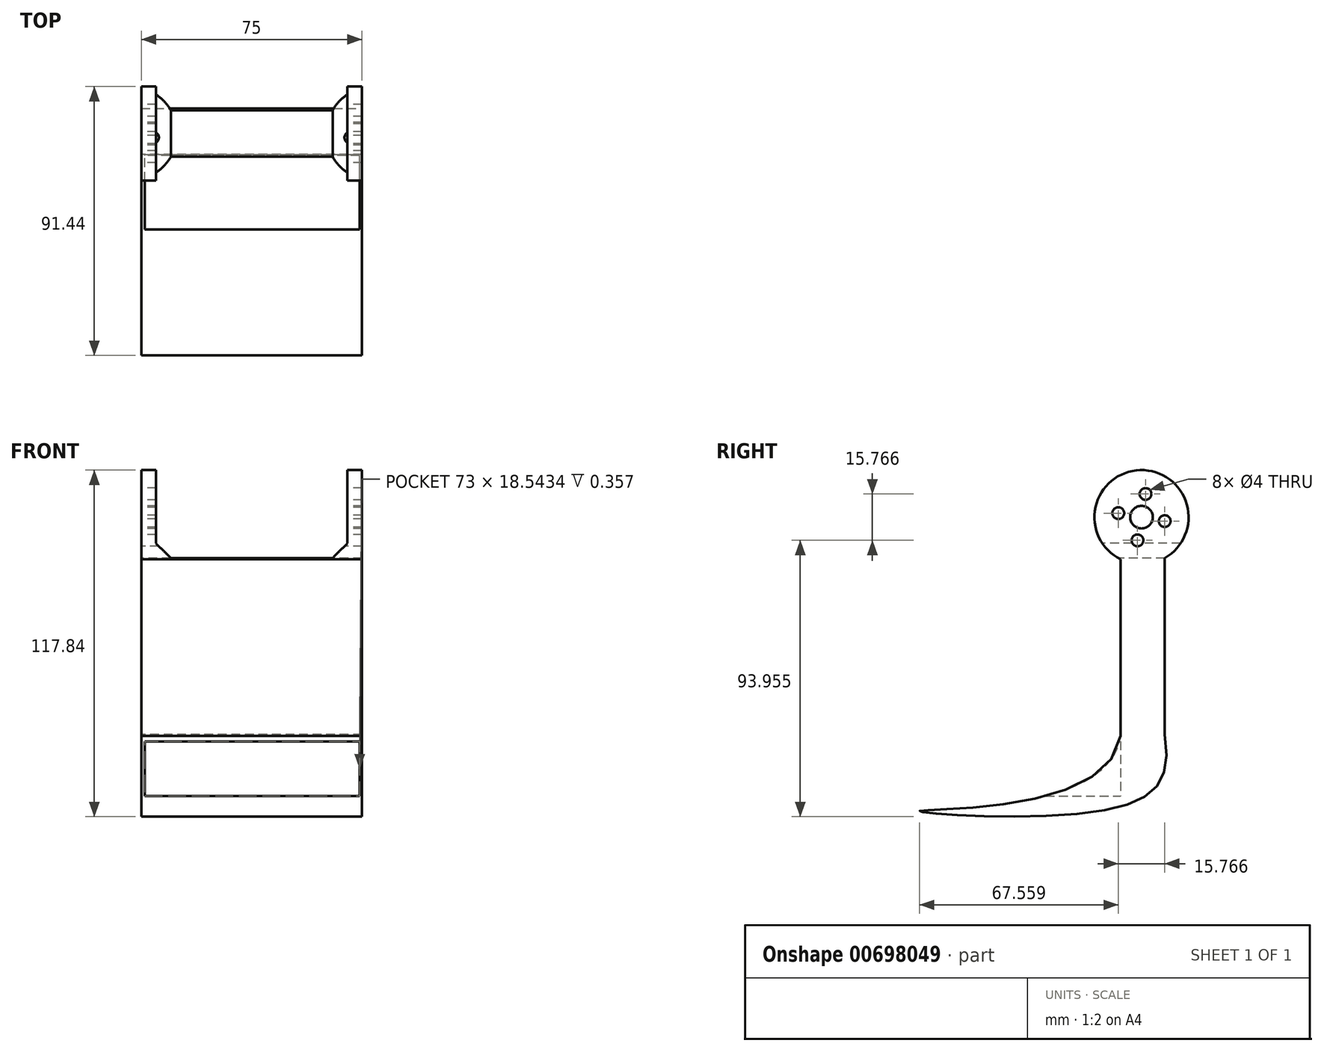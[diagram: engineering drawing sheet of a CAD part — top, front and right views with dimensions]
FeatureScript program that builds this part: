
annotation { "Feature Type Name" : "Feature", "Feature Type Description" : "" }
export const myFeature = defineFeature(function(context is Context, id is Id, definition is map)
    precondition{}
    {
        {
            var Q0;
            Q0=qCreatedBy(makeId("Right.planeOp"),FACE);
            var sketch = newSketch(context, id + "F0", { "sketchPlane" : qUnion([Q0])});
            skCircle(sketch, "E0", {"center": v(25.13, 34.1) * mm, "radius": 2 * mm});
            skCircle(sketch, "E1.1.0", {"center": v(15.88, 27.57) * mm, "radius": 2 * mm});
            skCircle(sketch, "E1.2.0", {"center": v(22.4, 18.33) * mm, "radius": 2 * mm});
            skCircle(sketch, "E1.3.0", {"center": v(31.64, 24.84) * mm, "radius": 2 * mm});
            skPoint(sketch, "E1.center", {"position": v(23.76, 26.2) * mm});
            skCircle(sketch, "E2", {"center": v(23.76, 26.2) * mm, "radius": 3.86 * mm});
            skCircle(sketch, "E3", {"center": v(23.76, 26.2) * mm, "radius": 16 * mm});
            skLineSegment(sketch, "E4", {"start": v(31.67, 12.3) * mm, "end": v(31.67, -47.7) * mm});
            skLineSegment(sketch, "E5", {"start": v(16.67, 11.87) * mm, "end": v(16.67, -48.13) * mm});
            skFitSpline(sketch, "E6", {"points": [v(31.67, -47.7) * mm, v(12.27, -73.3) * mm, v(-51.4, -73.65) * mm, v(16.67, -48.13) * mm], "startDerivative": vector(31.75, -179.08) * mm, "endDerivative": vector(26.2, 205.27) * mm});
            skSolve(sketch);
        }
        {
            var Q0;
            Q0 = qSketchRegion(id + "F0", true);
            extrude(context, id + "F1", {"entities" : qUnion([Q0]), "depth" : 75 * mm, "offsetDistance" : 25 * mm});
        }
        {
            var Q0;
            Q0=qCreatedBy(makeId("Front.planeOp"),FACE);
            var sketch = newSketch(context, id + "F2", { "sketchPlane" : qUnion([Q0])});
            skLineSegment(sketch, "E7", {"start": v(0, 42.2) * mm, "end": v(60, 42.2) * mm, "construction": true});
            skLineSegment(sketch, "E8.bottom", {"start": v(70, 42.2) * mm, "end": v(5, 42.2) * mm});
            skLineSegment(sketch, "E8.top", {"start": v(70, 12.3) * mm, "end": v(5, 12.3) * mm});
            skLineSegment(sketch, "E8.left", {"start": v(70, 42.2) * mm, "end": v(70, 12.3) * mm});
            skLineSegment(sketch, "E8.right", {"start": v(5, 42.2) * mm, "end": v(5, 12.3) * mm});
            skLineSegment(sketch, "E9.0", {"start": v(75, 12.3) * mm, "end": v(0, 12.3) * mm, "construction": true});
            skSolve(sketch);
        }
        {
            var Q0;
            Q0=makeQuery(id+"F2.imprint","IMPRINT",FACE,{"disambiguationData":[TD([[makeQuery(id+"F2.imprint","IMPRINT",EDGE,{"derivedFrom":sQuery(id+"F2.wireOp",EDGE,"E8.bottom")}),1.0]])]});
            extrude(context, id + "F3", {"entities" : qUnion([Q0]), "operationType" : NewBodyOperationType.REMOVE, "oppositeDirection" : true, "depth" : 50 * mm, "offsetDistance" : 25 * mm});
        }
        {
            var Q0;
            Q0=makeQuery(id+"F1.opExtrude","SWEPT_FACE",FACE,{"disambiguationData":[OSD([sQuery(id+"F0.wireOp",EDGE,"E5")])]});
            var sketch = newSketch(context, id + "F4", { "sketchPlane" : qUnion([Q0])});
            skLineSegment(sketch, "E10.bottom", {"start": v(1.15, -50.05) * mm, "end": v(74.15, -50.05) * mm});
            skLineSegment(sketch, "E10.top", {"start": v(1.15, -68.6) * mm, "end": v(74.15, -68.6) * mm});
            skLineSegment(sketch, "E10.left", {"start": v(1.15, -50.05) * mm, "end": v(1.15, -68.6) * mm});
            skLineSegment(sketch, "E10.right", {"start": v(74.15, -50.05) * mm, "end": v(74.15, -68.6) * mm});
            skFitSpline(sketch, "E11.0", {"points": [v(0, -42.99) * mm, v(0, -54.25) * mm, v(0, -65.5) * mm, v(0, -76.77) * mm]});
            skSolve(sketch);
        }
        {
            var Q0;
            Q0=makeQuery(id+"F4.imprint","IMPRINT",FACE,{"disambiguationData":[TD([[makeQuery(id+"F4.imprint","IMPRINT",EDGE,{"derivedFrom":sQuery(id+"F4.wireOp",EDGE,"E10.bottom")}),-1.0]])]});
            extrude(context, id + "F5", {"entities" : qUnion([Q0]), "operationType" : NewBodyOperationType.REMOVE, "depth" : 190.8 * mm, "offsetDistance" : 25 * mm});
        }
        {
            var Q0;
            {var subQ0=sQuery(id+"F2.wireOp",EDGE,"E8.top");var subQ1=sQuery(id+"F2.wireOp",EDGE,"E8.right");Q0=makeQuery(id+"F3.boolean.opBoolean","COPY",EDGE,{"disambiguationData":[TD([makeQuery(id+"F1.opExtrude","SWEPT_FACE",FACE,{"disambiguationData":[OSD([sQuery(id+"F0.wireOp",EDGE,"E1.2.0")])]}),makeQuery(id+"F1.opExtrude","SWEPT_FACE",FACE,{"disambiguationData":[OSD([sQuery(id+"F0.wireOp",EDGE,"E3")])]}),makeQuery(id+"F1.opExtrude","SWEPT_FACE",FACE,{"disambiguationData":[OSD([sQuery(id+"F0.wireOp",EDGE,"E4")])]}),makeQuery(id+"F3.opExtrude","SWEPT_FACE",FACE,{"disambiguationData":[OSD([subQ0])]}),makeQuery(id+"F3.opExtrude","SWEPT_FACE",FACE,{"disambiguationData":[OSD([subQ1])]})])],"derivedFrom":makeQuery(id+"F3.opExtrude","SWEPT_EDGE",EDGE,{"disambiguationData":[OSD([subQ0,subQ1])]})});}
            var Q1;
            {var subQ0=sQuery(id+"F2.wireOp",EDGE,"E8.top");var subQ1=sQuery(id+"F2.wireOp",EDGE,"E8.right");Q1=makeQuery(id+"F3.boolean.opBoolean","COPY",EDGE,{"disambiguationData":[TD([makeQuery(id+"F1.opExtrude","SWEPT_FACE",FACE,{"disambiguationData":[OSD([sQuery(id+"F0.wireOp",EDGE,"E1.2.0")])]}),makeQuery(id+"F1.opExtrude","SWEPT_FACE",FACE,{"disambiguationData":[OSD([sQuery(id+"F0.wireOp",EDGE,"E3")])]}),makeQuery(id+"F3.opExtrude","SWEPT_FACE",FACE,{"disambiguationData":[OSD([subQ0])]}),makeQuery(id+"F3.opExtrude","SWEPT_FACE",FACE,{"disambiguationData":[OSD([subQ1])]})])],"derivedFrom":makeQuery(id+"F3.opExtrude","SWEPT_EDGE",EDGE,{"disambiguationData":[OSD([subQ0,subQ1])]})});}
            var Q2;
            {var subQ0=sQuery(id+"F2.wireOp",EDGE,"E8.top");var subQ1=sQuery(id+"F2.wireOp",EDGE,"E8.left");Q2=makeQuery(id+"F3.boolean.opBoolean","COPY",EDGE,{"disambiguationData":[TD([makeQuery(id+"F1.opExtrude","SWEPT_FACE",FACE,{"disambiguationData":[OSD([sQuery(id+"F0.wireOp",EDGE,"E1.2.0")])]}),makeQuery(id+"F1.opExtrude","SWEPT_FACE",FACE,{"disambiguationData":[OSD([sQuery(id+"F0.wireOp",EDGE,"E3")])]}),makeQuery(id+"F1.opExtrude","SWEPT_FACE",FACE,{"disambiguationData":[OSD([sQuery(id+"F0.wireOp",EDGE,"E4")])]}),makeQuery(id+"F3.opExtrude","SWEPT_FACE",FACE,{"disambiguationData":[OSD([subQ0])]}),makeQuery(id+"F3.opExtrude","SWEPT_FACE",FACE,{"disambiguationData":[OSD([subQ1])]})])],"derivedFrom":makeQuery(id+"F3.opExtrude","SWEPT_EDGE",EDGE,{"disambiguationData":[OSD([subQ0,subQ1])]})});}
            var Q3;
            {var subQ0=sQuery(id+"F2.wireOp",EDGE,"E8.left");var subQ1=sQuery(id+"F2.wireOp",EDGE,"E8.top");Q3=makeQuery(id+"F3.boolean.opBoolean","COPY",EDGE,{"disambiguationData":[TD([makeQuery(id+"F1.opExtrude","SWEPT_FACE",FACE,{"disambiguationData":[OSD([sQuery(id+"F0.wireOp",EDGE,"E1.2.0")])]}),makeQuery(id+"F1.opExtrude","SWEPT_FACE",FACE,{"disambiguationData":[OSD([sQuery(id+"F0.wireOp",EDGE,"E3")])]}),makeQuery(id+"F3.opExtrude","SWEPT_FACE",FACE,{"disambiguationData":[OSD([subQ1])]}),makeQuery(id+"F3.opExtrude","SWEPT_FACE",FACE,{"disambiguationData":[OSD([subQ0])]})])],"derivedFrom":makeQuery(id+"F3.opExtrude","SWEPT_EDGE",EDGE,{"disambiguationData":[OSD([subQ1,subQ0])]})});}
            chamfer(context, id + "F6", {"entities" : qUnion([Q0, Q1, Q2, Q3]), "width" : 5 * mm, "tangentPropagation" : true});
        }
    });
